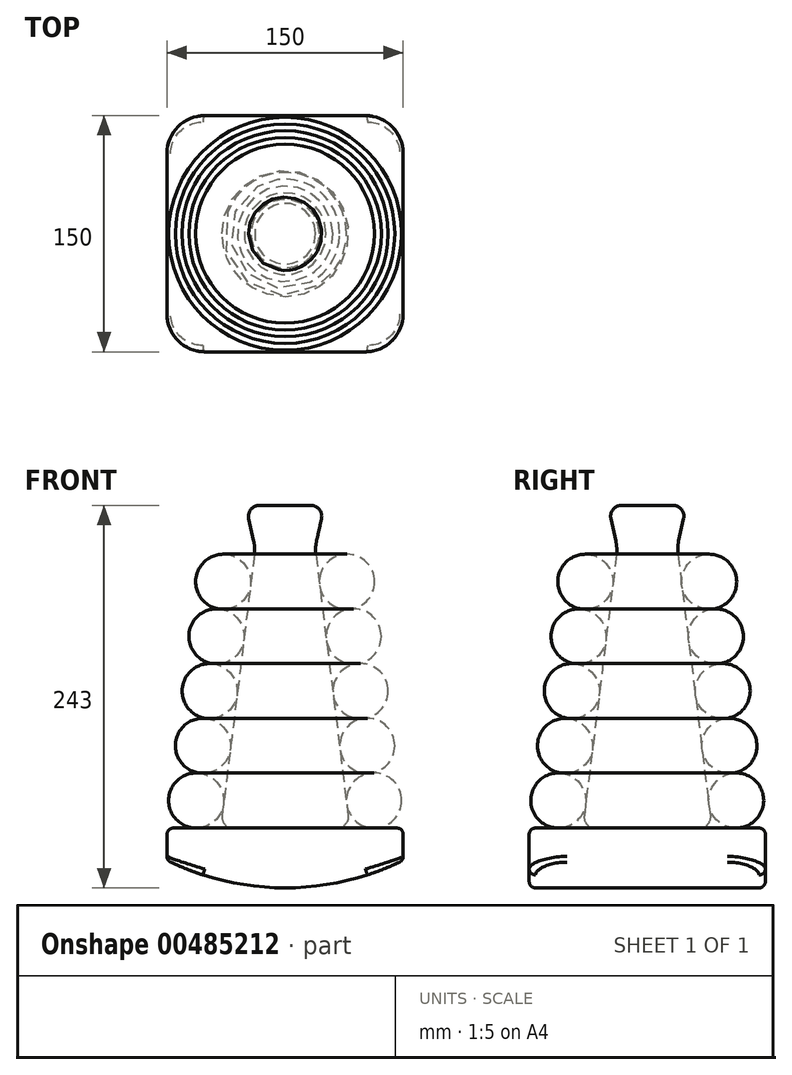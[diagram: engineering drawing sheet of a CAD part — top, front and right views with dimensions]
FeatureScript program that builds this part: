
annotation { "Feature Type Name" : "Feature", "Feature Type Description" : "" }
export const myFeature = defineFeature(function(context is Context, id is Id, definition is map)
    precondition{}
    {
        {
            var Q0;
            Q0=qCreatedBy(makeId("Front.planeOp"),FACE);
            var sketch = newSketch(context, id + "F0", { "sketchPlane" : qUnion([Q0])});
            skLineSegment(sketch, "E0.bottom", {"start": v(-75, 0) * mm, "end": v(75, 0) * mm});
            skLineSegment(sketch, "E0.top", {"start": v(-75, 38) * mm, "end": v(75, 38) * mm});
            skLineSegment(sketch, "E0.left", {"start": v(-75, 0) * mm, "end": v(-75, 38) * mm});
            skLineSegment(sketch, "E0.right", {"start": v(75, 0) * mm, "end": v(75, 38) * mm});
            skArc(sketch, "E1.converted", {"start": v(-75, 17.44) * mm, "mid": v(0, 0) * mm, "end": v(75, 17.44) * mm});
            skLineSegment(sketch, "E2", {"start": v(-25, 243) * mm, "end": v(0, 243) * mm});
            skLineSegment(sketch, "E3", {"start": v(0, 243) * mm, "end": v(0, 38) * mm});
            skLineSegment(sketch, "E4", {"start": v(-25, 243) * mm, "end": v(-19, 216) * mm});
            skLineSegment(sketch, "E5", {"start": v(-19, 216) * mm, "end": v(-41, 38) * mm});
            skCircle(sketch, "E6", {"center": v(-56.47, 55.5) * mm, "radius": 17.5 * mm});
            skCircle(sketch, "E7", {"center": v(-52.18, 90.24) * mm, "radius": 17.5 * mm});
            skCircle(sketch, "E8", {"center": v(-47.88, 124.97) * mm, "radius": 17.5 * mm});
            skCircle(sketch, "E9", {"center": v(-43.6, 159.7) * mm, "radius": 17.5 * mm});
            skCircle(sketch, "E10", {"center": v(-39.3, 194.44) * mm, "radius": 17.5 * mm});
            skSolve(sketch);
        }
        {
            var Q0;
            {var subQ1=sQuery(id+"F0.wireOp",EDGE,"E0.top");var subQ6=sQuery(id+"F0.wireOp",EDGE,"E0.left");var subQ7=makeQuery(id+"F0.imprint","INTERSECT",VERTEX,{"derivedFrom":[subQ1,subQ6]});Q0=makeQuery(id+"F0.imprint","IMPRINT",FACE,{"disambiguationData":[TD([[makeQuery(id+"F0.imprint","IMPRINT",EDGE,{"disambiguationData":[TD([[subQ7,-1.0]])],"derivedFrom":subQ1}),-1.0]])]});}
            extrude(context, id + "F1", {"entities" : qUnion([Q0]), "endBound" : BoundingType.SYMMETRIC, "depth" : 150 * mm});
        }
        {
            var Q0;
            Q0=makeQuery(id+"F0.imprint","IMPRINT",FACE,{"disambiguationData":[TD([[makeQuery(id+"F0.imprint","IMPRINT",EDGE,{"derivedFrom":sQuery(id+"F0.wireOp",EDGE,"E2")}),-1.0]])]});
            var Q1;
            {var subQ0=sQuery(id+"F0.wireOp",EDGE,"E6");var subQ1=makeQuery(id+"F0.imprint","INTERSECT",VERTEX,{"derivedFrom":[sQuery(id+"F0.wireOp",EDGE,"E0.top"),subQ0]});Q1=makeQuery(id+"F0.imprint","IMPRINT",FACE,{"disambiguationData":[TD([[makeQuery(id+"F0.imprint","IMPRINT",EDGE,{"disambiguationData":[TD([[subQ1,1.0]])],"derivedFrom":subQ0}),1.0]])]});}
            var Q2;
            {var subQ0=sQuery(id+"F0.wireOp",EDGE,"E7");var subQ1=makeQuery(id+"F0.imprint","INTERSECT",VERTEX,{"derivedFrom":[sQuery(id+"F0.wireOp",EDGE,"E6"),subQ0]});Q2=makeQuery(id+"F0.imprint","IMPRINT",FACE,{"disambiguationData":[TD([[makeQuery(id+"F0.imprint","IMPRINT",EDGE,{"disambiguationData":[TD([[subQ1,1.0]])],"derivedFrom":subQ0}),1.0]])]});}
            var Q3;
            {var subQ0=sQuery(id+"F0.wireOp",EDGE,"E8");var subQ1=makeQuery(id+"F0.imprint","INTERSECT",VERTEX,{"derivedFrom":[sQuery(id+"F0.wireOp",EDGE,"E7"),subQ0]});Q3=makeQuery(id+"F0.imprint","IMPRINT",FACE,{"disambiguationData":[TD([[makeQuery(id+"F0.imprint","IMPRINT",EDGE,{"disambiguationData":[TD([[subQ1,1.0]])],"derivedFrom":subQ0}),1.0]])]});}
            var Q4;
            {var subQ0=sQuery(id+"F0.wireOp",EDGE,"E9");var subQ1=makeQuery(id+"F0.imprint","INTERSECT",VERTEX,{"derivedFrom":[sQuery(id+"F0.wireOp",EDGE,"E8"),subQ0]});Q4=makeQuery(id+"F0.imprint","IMPRINT",FACE,{"disambiguationData":[TD([[makeQuery(id+"F0.imprint","IMPRINT",EDGE,{"disambiguationData":[TD([[subQ1,1.0]])],"derivedFrom":subQ0}),1.0]])]});}
            var Q5;
            {var subQ0=sQuery(id+"F0.wireOp",EDGE,"E10");var subQ1=makeQuery(id+"F0.imprint","INTERSECT",VERTEX,{"derivedFrom":[sQuery(id+"F0.wireOp",EDGE,"E5"),subQ0]});Q5=makeQuery(id+"F0.imprint","IMPRINT",FACE,{"disambiguationData":[TD([[makeQuery(id+"F0.imprint","IMPRINT",EDGE,{"disambiguationData":[TD([[subQ1,1.0]])],"derivedFrom":subQ0}),1.0]])]});}
            var Q6;
            Q6=sQuery(id+"F0.wireOp",EDGE,"E3");
            revolve(context, id + "F2", {"entities" : qUnion([Q0, Q1, Q2, Q3, Q4, Q5]), "axis" : qUnion([Q6]), "revolveType" : RevolveType.FULL});
        }
        {
            var Q0;
            Q0=makeQuery(id+"F1.opExtrude","CAP_EDGE",EDGE,{"disambiguationData":[OSD([sQuery(id+"F0.wireOp",EDGE,"E0.left")])],"isStart":false});
            var Q1;
            Q1=makeQuery(id+"F1.opExtrude","CAP_EDGE",EDGE,{"disambiguationData":[OSD([sQuery(id+"F0.wireOp",EDGE,"E0.right")])],"isStart":true});
            var Q2;
            Q2=makeQuery(id+"F1.opExtrude","CAP_EDGE",EDGE,{"disambiguationData":[OSD([sQuery(id+"F0.wireOp",EDGE,"E0.left")])],"isStart":true});
            var Q3;
            Q3=makeQuery(id+"F1.opExtrude","CAP_EDGE",EDGE,{"disambiguationData":[OSD([sQuery(id+"F0.wireOp",EDGE,"E0.right")])],"isStart":false});
            fillet(context, id + "F3", {"entities" : qUnion([Q0, Q1, Q2, Q3]), "radius" : 24 * mm, "tangentPropagation" : true, "allowEdgeOverflow" : false});
        }
        {
            var Q0;
            Q0=makeQuery(id+"F1.opExtrude","CAP_EDGE",EDGE,{"disambiguationData":[OSD([sQuery(id+"F0.wireOp",EDGE,"E0.top")])],"isStart":false});
            var Q1;
            Q1=makeQuery(id+"F1.opExtrude","CAP_EDGE",EDGE,{"disambiguationData":[OSD([sQuery(id+"F0.wireOp",EDGE,"E1.converted")])],"isStart":false});
            fillet(context, id + "F4", {"entities" : qUnion([Q0, Q1]), "radius" : 4 * mm, "tangentPropagation" : true, "allowEdgeOverflow" : false});
        }
        {
            var Q0;
            Q0=makeQuery(id+"F2.opRevolve","SWEPT_EDGE",EDGE,{"disambiguationData":[OSD([sQuery(id+"F0.wireOp",EDGE,"E0.top"),sQuery(id+"F0.wireOp",EDGE,"E5")])]});
            var Q1;
            Q1=makeQuery(id+"F2.opRevolve","SWEPT_EDGE",EDGE,{"disambiguationData":[OSD([sQuery(id+"F0.wireOp",EDGE,"E2"),sQuery(id+"F0.wireOp",EDGE,"E4")])]});
            fillet(context, id + "F5", {"entities" : qUnion([Q0, Q1]), "radius" : 7 * mm, "tangentPropagation" : true, "allowEdgeOverflow" : false});
        }
        {
            var Q0;
            Q0=makeQuery(id+"F2.opRevolve","SWEPT_EDGE",EDGE,{"disambiguationData":[OSD([sQuery(id+"F0.wireOp",EDGE,"E4"),sQuery(id+"F0.wireOp",EDGE,"E5")])]});
            fillet(context, id + "F6", {"entities" : qUnion([Q0]), "radius" : 25 * mm, "tangentPropagation" : true, "allowEdgeOverflow" : false});
        }
    });
